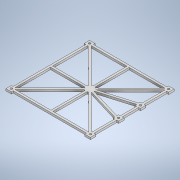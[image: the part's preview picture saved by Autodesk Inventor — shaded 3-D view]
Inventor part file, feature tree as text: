
AUTODESK INVENTOR PART (.ipt)
format: ipt  version: 2020 (Build 240168000, 168)  size: 265,216 bytes
history: native  units: in
note: dims shown in document units (in); Inventor stores cm internally (conversion verified against a paired STEP export)
features: extrude x1, sketch x1
ambient origin geometry x8: Origin, YZ Plane, XZ Plane, XY Plane, X Axis, Y Axis, Z Axis, Center Point
bodies: Solid1 (feature_tree)
feature tree (2):
  extrude  "Extrusion1"  Depth=0.1181in
  sketch  "Sketch1"  dims[d0=5.9055in d1=5.1181in d2=0.5114in d3=0.0157in d4=0.1575in d5=0.315in d6=0.315in d7=0.315in d8=0.315in d9=0.4724in d10=0.122in d11=0.122in d13=0.4724in d14=0.1181in d15=0.1181in d16=0.1181in d17=0.1181in d18=0.1181in d19=0.1181in d20=0.1181in d21=0.1181in d22=0.1181in d23=0.1181in d24=0.1181in d25=0.1181in d26=0.1181in d27=0.0in]
